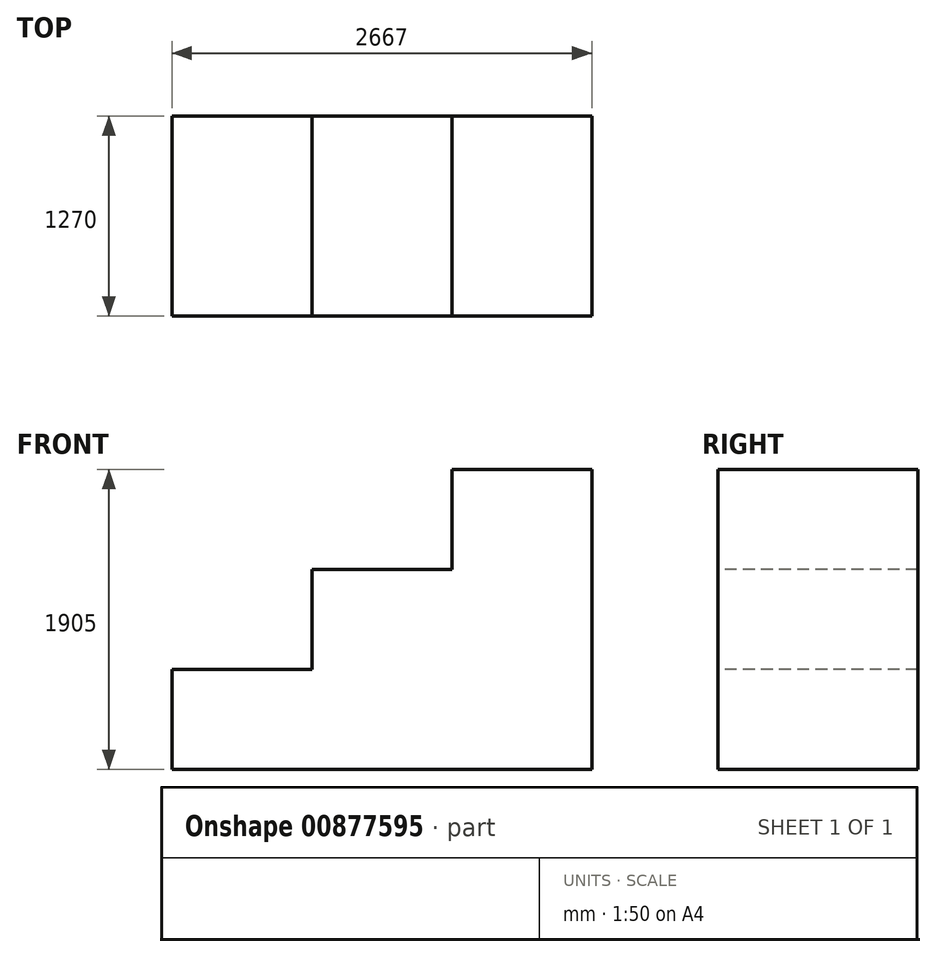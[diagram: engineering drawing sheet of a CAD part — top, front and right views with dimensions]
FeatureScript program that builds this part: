
annotation { "Feature Type Name" : "Feature", "Feature Type Description" : "" }
export const myFeature = defineFeature(function(context is Context, id is Id, definition is map)
    precondition{}
    {
        {
            var Q0;
            Q0=qCreatedBy(makeId("Top.planeOp"),FACE);
            var sketch = newSketch(context, id + "F0", { "sketchPlane" : qUnion([Q0])});
            skLineSegment(sketch, "E0.bottom", {"start": v(0, 0) * mm, "end": v(-2667, 0) * mm});
            skLineSegment(sketch, "E0.top", {"start": v(0, -1270) * mm, "end": v(-2667, -1270) * mm});
            skLineSegment(sketch, "E0.left", {"start": v(0, 0) * mm, "end": v(0, -1270) * mm});
            skLineSegment(sketch, "E0.right", {"start": v(-2667, 0) * mm, "end": v(-2667, -1270) * mm});
            skSolve(sketch);
        }
        {
            var Q0;
            Q0=makeQuery(id+"F0.imprint","IMPRINT",FACE,{"disambiguationData":[TD([[makeQuery(id+"F0.imprint","IMPRINT",EDGE,{"derivedFrom":sQuery(id+"F0.wireOp",EDGE,"E0.bottom")}),1.0]])]});
            extrude(context, id + "F1", {"entities" : qUnion([Q0]), "depth" : 1905 * mm, "offsetDistance" : 25.4 * mm});
        }
        {
            var Q0;
            Q0=makeQuery(id+"F1.opExtrude","CAP_FACE",FACE,{"disambiguationData":[OSD([sQuery(id+"F0.wireOp",EDGE,"E0.bottom"),sQuery(id+"F0.wireOp",EDGE,"E0.top"),sQuery(id+"F0.wireOp",EDGE,"E0.left"),sQuery(id+"F0.wireOp",EDGE,"E0.right")])],"isStart":false});
            var sketch = newSketch(context, id + "F2", { "sketchPlane" : qUnion([Q0])});
            skLineSegment(sketch, "E1.bottom", {"start": v(-2667, 0) * mm, "end": v(-1778, 0) * mm});
            skLineSegment(sketch, "E1.top", {"start": v(-2667, -1270) * mm, "end": v(-1778, -1270) * mm});
            skLineSegment(sketch, "E1.left", {"start": v(-2667, 0) * mm, "end": v(-2667, -1270) * mm});
            skLineSegment(sketch, "E1.right", {"start": v(-1778, 0) * mm, "end": v(-1778, -1270) * mm});
            skSolve(sketch);
        }
        {
            var Q0;
            Q0=makeQuery(id+"F2.imprint","IMPRINT",FACE,{"disambiguationData":[TD([[makeQuery(id+"F2.imprint","IMPRINT",EDGE,{"derivedFrom":sQuery(id+"F2.wireOp",EDGE,"E1.bottom")}),1.0]])]});
            extrude(context, id + "F3", {"entities" : qUnion([Q0]), "operationType" : NewBodyOperationType.ADD, "oppositeDirection" : true, "depth" : 1270 * mm, "offsetDistance" : 25.4 * mm});
        }
        {
            var Q0;
            Q0=makeQuery(id+"F1.opExtrude","SWEPT_FACE",FACE,{"disambiguationData":[OSD([sQuery(id+"F0.wireOp",EDGE,"E0.top")])]});
            var sketch = newSketch(context, id + "F4", { "sketchPlane" : qUnion([Q0])});
            skLineSegment(sketch, "E2.bottom", {"start": v(-2667, 1905) * mm, "end": v(-1778, 1905) * mm});
            skLineSegment(sketch, "E2.top", {"start": v(-2667, 635) * mm, "end": v(-1778, 635) * mm});
            skLineSegment(sketch, "E2.left", {"start": v(-2667, 1905) * mm, "end": v(-2667, 635) * mm});
            skLineSegment(sketch, "E2.right", {"start": v(-1778, 1905) * mm, "end": v(-1778, 635) * mm});
            skSolve(sketch);
        }
        {
            var Q0;
            Q0=makeQuery(id+"F4.imprint","IMPRINT",FACE,{"disambiguationData":[TD([[makeQuery(id+"F4.imprint","IMPRINT",EDGE,{"derivedFrom":sQuery(id+"F4.wireOp",EDGE,"E2.bottom")}),1.0]])]});
            extrude(context, id + "F5", {"entities" : qUnion([Q0]), "operationType" : NewBodyOperationType.REMOVE, "oppositeDirection" : true, "depth" : 2707.64 * mm, "offsetDistance" : 25.4 * mm});
        }
        {
            var Q0;
            Q0=makeQuery(id+"F1.opExtrude","SWEPT_FACE",FACE,{"disambiguationData":[OSD([sQuery(id+"F0.wireOp",EDGE,"E0.top")])]});
            var sketch = newSketch(context, id + "F6", { "sketchPlane" : qUnion([Q0])});
            skLineSegment(sketch, "E3.bottom", {"start": v(-1778, 1905) * mm, "end": v(-889, 1905) * mm});
            skLineSegment(sketch, "E3.top", {"start": v(-1778, 1270) * mm, "end": v(-889, 1270) * mm});
            skLineSegment(sketch, "E3.left", {"start": v(-1778, 1905) * mm, "end": v(-1778, 1270) * mm});
            skLineSegment(sketch, "E3.right", {"start": v(-889, 1905) * mm, "end": v(-889, 1270) * mm});
            skSolve(sketch);
        }
        {
            var Q0;
            Q0=makeQuery(id+"F6.imprint","IMPRINT",FACE,{"disambiguationData":[TD([[makeQuery(id+"F6.imprint","IMPRINT",EDGE,{"derivedFrom":sQuery(id+"F6.wireOp",EDGE,"E3.bottom")}),1.0]])]});
            extrude(context, id + "F7", {"entities" : qUnion([Q0]), "operationType" : NewBodyOperationType.REMOVE, "oppositeDirection" : true, "depth" : 2806.7 * mm, "offsetDistance" : 25.4 * mm});
        }
    });
